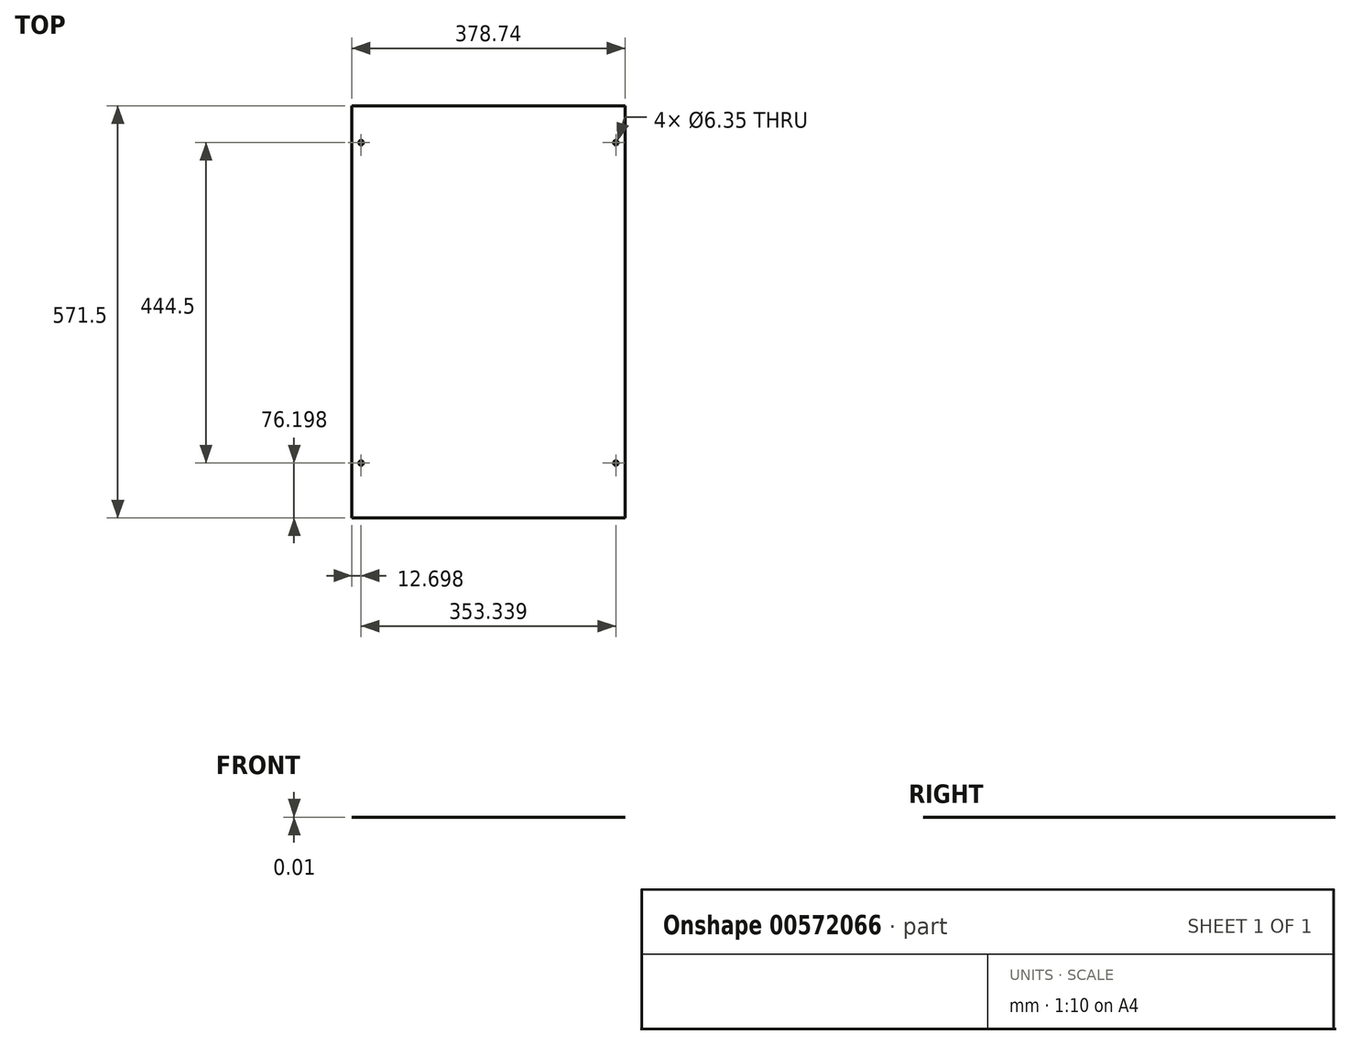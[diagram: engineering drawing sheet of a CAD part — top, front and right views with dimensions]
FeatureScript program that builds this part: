
annotation { "Feature Type Name" : "Feature", "Feature Type Description" : "" }
export const myFeature = defineFeature(function(context is Context, id is Id, definition is map)
    precondition{}
    {
        {
            var Q0;
            Q0=qCreatedBy(makeId("Top.planeOp"),FACE);
            var sketch = newSketch(context, id + "F0", { "sketchPlane" : qUnion([Q0])});
            skLineSegment(sketch, "E0.bottom", {"start": v(167.29, -85.72) * mm, "end": v(-211.45, -85.72) * mm});
            skLineSegment(sketch, "E0.top", {"start": v(167.29, 485.78) * mm, "end": v(-211.45, 485.78) * mm});
            skLineSegment(sketch, "E0.left", {"start": v(167.29, -85.72) * mm, "end": v(167.29, 485.78) * mm});
            skLineSegment(sketch, "E0.right", {"start": v(-211.45, -85.72) * mm, "end": v(-211.45, 485.78) * mm});
            skPoint(sketch, "E0.middle", {"position": v(-22.08, 200.03) * mm});
            skSolve(sketch);
        }
        {
            var Q0;
            Q0 = qSketchRegion(id + "F0", true);
            extrude(context, id + "F1", {"entities" : qUnion([Q0]), "depth" : 1 / 101.6 * mm, "offsetDistance" : 25.4 * mm});
        }
        {
            var Q0;
            Q0=makeQuery(id+"F1.opExtrude","CAP_FACE",FACE,{"disambiguationData":[OSD([sQuery(id+"F0.wireOp",EDGE,"E0.bottom"),sQuery(id+"F0.wireOp",EDGE,"E0.top"),sQuery(id+"F0.wireOp",EDGE,"E0.left"),sQuery(id+"F0.wireOp",EDGE,"E0.right")])],"isStart":false});
            var sketch = newSketch(context, id + "F2", { "sketchPlane" : qUnion([Q0])});
            skCircle(sketch, "E1", {"center": v(-198.75, 434.98) * mm, "radius": 3.17 * mm});
            skCircle(sketch, "E2", {"center": v(154.59, 434.98) * mm, "radius": 3.17 * mm});
            skCircle(sketch, "E3", {"center": v(-198.75, -9.52) * mm, "radius": 3.18 * mm});
            skCircle(sketch, "E4", {"center": v(154.59, -9.52) * mm, "radius": 3.18 * mm});
            skLineSegment(sketch, "E5", {"start": v(-198.75, 434.98) * mm, "end": v(-195.68, 435.78) * mm});
            skLineSegment(sketch, "E6", {"start": v(154.59, 434.98) * mm, "end": v(154.59, 438.15) * mm});
            skLineSegment(sketch, "E7", {"start": v(-198.75, -9.52) * mm, "end": v(-198.75, -6.35) * mm});
            skLineSegment(sketch, "E8", {"start": v(154.59, -9.52) * mm, "end": v(154.59, -6.35) * mm});
            skLineSegment(sketch, "E9", {"start": v(-211.45, 434.98) * mm, "end": v(-198.75, 434.98) * mm});
            skLineSegment(sketch, "E10", {"start": v(-198.75, 434.98) * mm, "end": v(-198.75, 485.78) * mm});
            skLineSegment(sketch, "E11", {"start": v(154.59, 485.78) * mm, "end": v(154.59, 434.98) * mm});
            skLineSegment(sketch, "E12", {"start": v(167.29, 434.98) * mm, "end": v(154.59, 434.98) * mm});
            skLineSegment(sketch, "E13", {"start": v(-211.45, -9.52) * mm, "end": v(-198.75, -9.52) * mm});
            skLineSegment(sketch, "E14", {"start": v(-198.75, -9.52) * mm, "end": v(-198.75, -85.72) * mm});
            skLineSegment(sketch, "E15", {"start": v(154.59, -9.52) * mm, "end": v(154.59, -85.72) * mm});
            skLineSegment(sketch, "E16", {"start": v(154.59, -9.52) * mm, "end": v(167.29, -9.52) * mm});
            skSolve(sketch);
        }
        {
            var Q0;
            Q0 = qSketchRegion(id + "F2", true);
            extrude(context, id + "F3", {"entities" : qUnion([Q0]), "operationType" : NewBodyOperationType.REMOVE, "endBound" : BoundingType.THROUGH_ALL, "oppositeDirection" : true, "depth" : 25.4 * mm, "offsetDistance" : 25.4 * mm});
        }
    });
